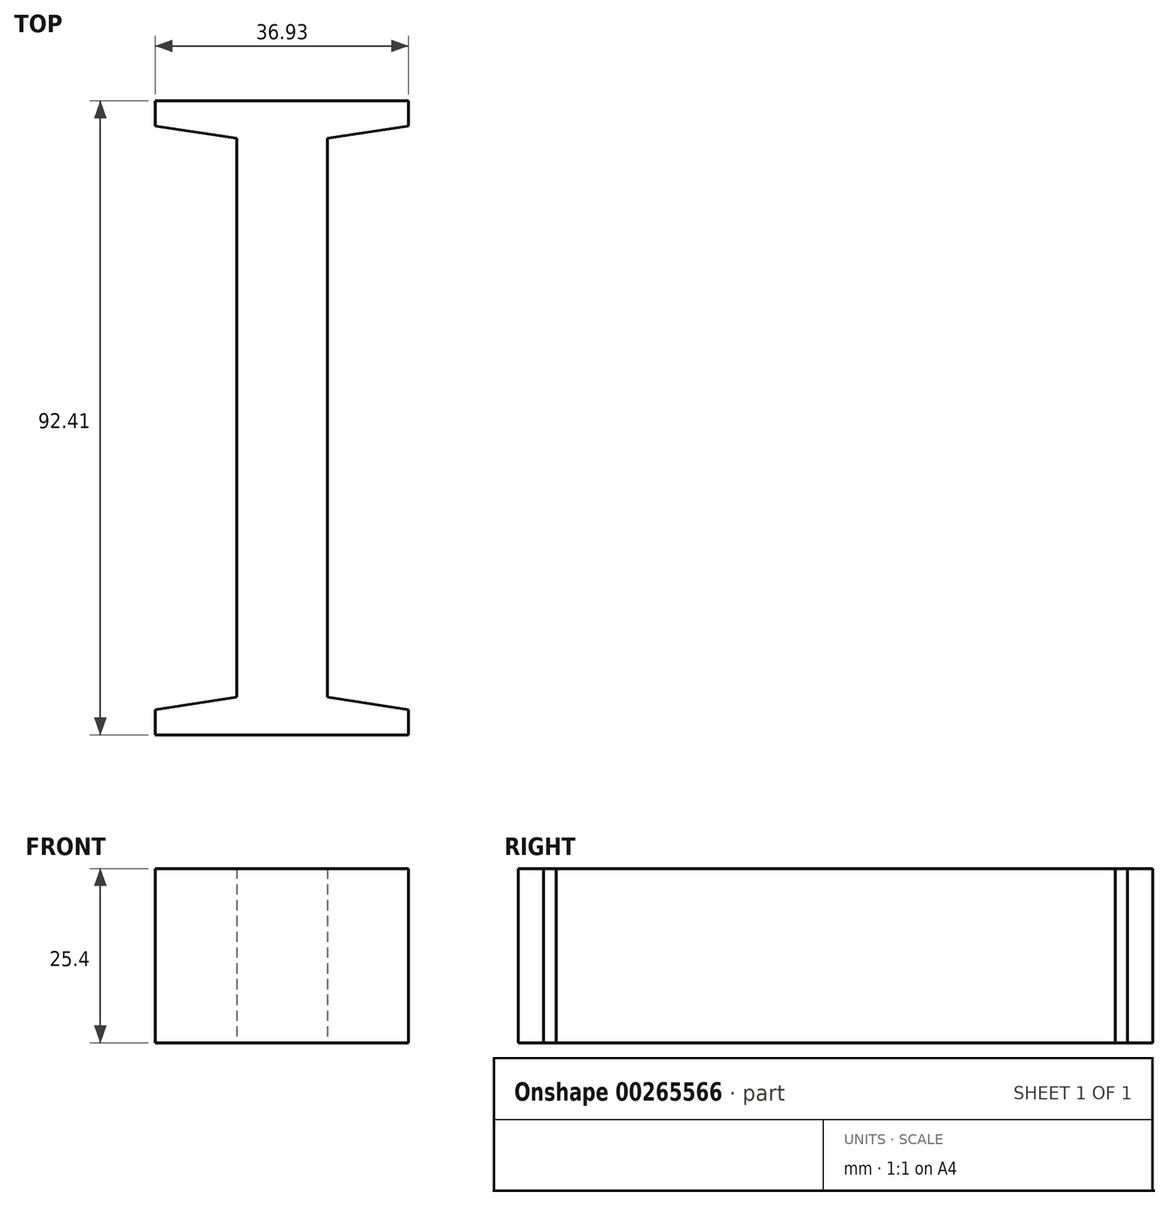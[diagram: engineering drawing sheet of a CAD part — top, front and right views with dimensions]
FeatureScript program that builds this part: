
annotation { "Feature Type Name" : "Feature", "Feature Type Description" : "" }
export const myFeature = defineFeature(function(context is Context, id is Id, definition is map)
    precondition{}
    {
        {
            var Q0;
            Q0=qCreatedBy(makeId("Top.planeOp"),FACE);
            var sketch = newSketch(context, id + "F0", { "sketchPlane" : qUnion([Q0])});
            skText(sketch, "E0", { "text": "I", "fontName": "Tinos-Regular.ttf"});
            const initialGuessF0  = {"E0": [-0.0259, -0.05822, 1, 0, 0.1016]};
            skSetInitialGuess(sketch, initialGuessF0);
            skSolve(sketch);
        }
        {
            var Q0;
            Q0 = qSketchRegion(id + "F0", true);
            extrude(context, id + "F1", {"entities" : qUnion([Q0]), "depth" : 25.4 * mm});
        }
    });
